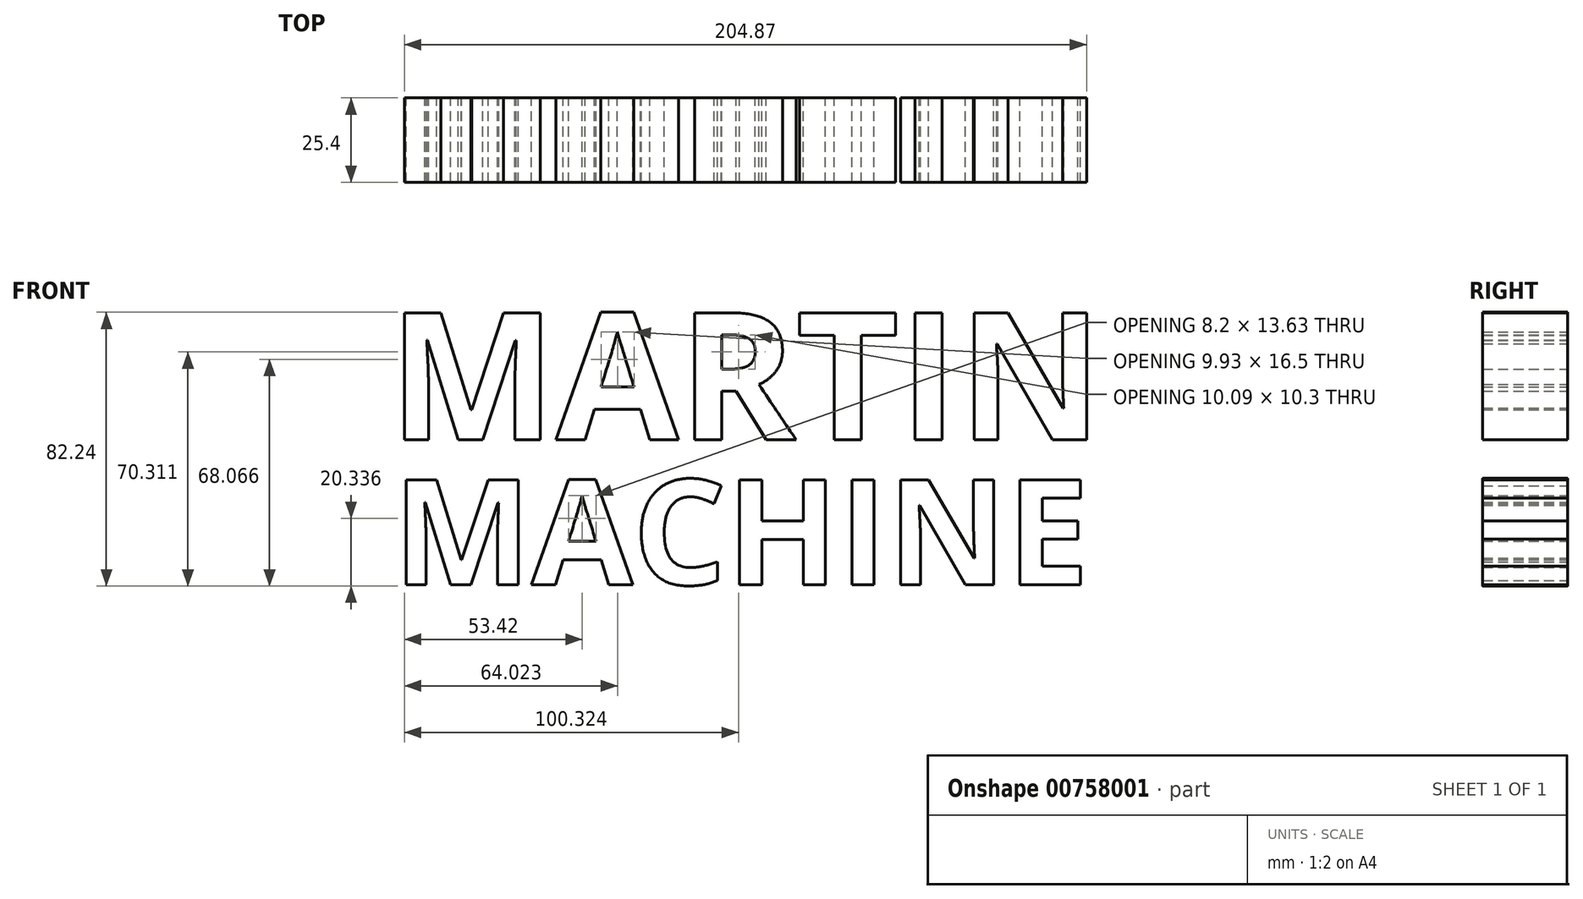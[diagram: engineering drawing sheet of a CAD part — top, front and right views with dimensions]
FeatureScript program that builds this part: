
annotation { "Feature Type Name" : "Feature", "Feature Type Description" : "" }
export const myFeature = defineFeature(function(context is Context, id is Id, definition is map)
    precondition{}
    {
        {
            var Q0;
            Q0=qCreatedBy(makeId("Front.planeOp"),FACE);
            var sketch = newSketch(context, id + "F0", { "sketchPlane" : qUnion([Q0])});
            skText(sketch, "E0", { "text": "MARTIN ", "fontName": "OpenSans-Bold.ttf"});
            const initialGuessF0  = {"E0": [-0.0641, 0.0153, 1, 0, 0.03845]};
            skSetInitialGuess(sketch, initialGuessF0);
            skSolve(sketch);
        }
        {
            var Q0;
            Q0=makeQuery(id+"F0.imprint","IMPRINT",FACE,{"disambiguationData":[TD([[makeQuery(id+"F0.imprint","IMPRINT",EDGE,{"derivedFrom":sQuery(id+"F0.wireOp",EDGE,"E0.sketch_text.stroke-0")}),-1.0]])]});
            var Q1;
            Q1=makeQuery(id+"F0.imprint","IMPRINT",FACE,{"disambiguationData":[TD([[makeQuery(id+"F0.imprint","IMPRINT",EDGE,{"derivedFrom":sQuery(id+"F0.wireOp",EDGE,"E0.sketch_text.stroke-19")}),-1.0]])]});
            var Q2;
            Q2=makeQuery(id+"F0.imprint","IMPRINT",FACE,{"disambiguationData":[TD([[makeQuery(id+"F0.imprint","IMPRINT",EDGE,{"derivedFrom":sQuery(id+"F0.wireOp",EDGE,"E0.sketch_text.stroke-31")}),-1.0]])]});
            var Q3;
            Q3=makeQuery(id+"F0.imprint","IMPRINT",FACE,{"disambiguationData":[TD([[makeQuery(id+"F0.imprint","IMPRINT",EDGE,{"derivedFrom":sQuery(id+"F0.wireOp",EDGE,"E0.sketch_text.stroke-50")}),-1.0]])]});
            var Q4;
            Q4=makeQuery(id+"F0.imprint","IMPRINT",FACE,{"disambiguationData":[TD([[makeQuery(id+"F0.imprint","IMPRINT",EDGE,{"derivedFrom":sQuery(id+"F0.wireOp",EDGE,"E0.sketch_text.stroke-58")}),-1.0]])]});
            var Q5;
            Q5=makeQuery(id+"F0.imprint","IMPRINT",FACE,{"disambiguationData":[TD([[makeQuery(id+"F0.imprint","IMPRINT",EDGE,{"derivedFrom":sQuery(id+"F0.wireOp",EDGE,"E0.sketch_text.stroke-62")}),-1.0]])]});
            extrude(context, id + "F1", {"entities" : qUnion([Q0, Q1, Q2, Q3, Q4, Q5]), "depth" : 25.4 * mm, "offsetDistance" : 25.4 * mm});
        }
        {
            var Q0;
            Q0=qCreatedBy(makeId("Front.planeOp"),FACE);
            var sketch = newSketch(context, id + "F2", { "sketchPlane" : qUnion([Q0])});
            skText(sketch, "E1", { "text": "MACHINE", "fontName": "OpenSans-Bold.ttf"});
            const initialGuessF2  = {"E1": [-0.06271, -0.02823, 1, 0, 0.03175]};
            skSetInitialGuess(sketch, initialGuessF2);
            skSolve(sketch);
        }
        {
            var Q0;
            Q0 = qSketchRegion(id + "F2", true);
            extrude(context, id + "F3", {"entities" : qUnion([Q0]), "depth" : 25.4 * mm, "offsetDistance" : 25.4 * mm});
        }
    });
